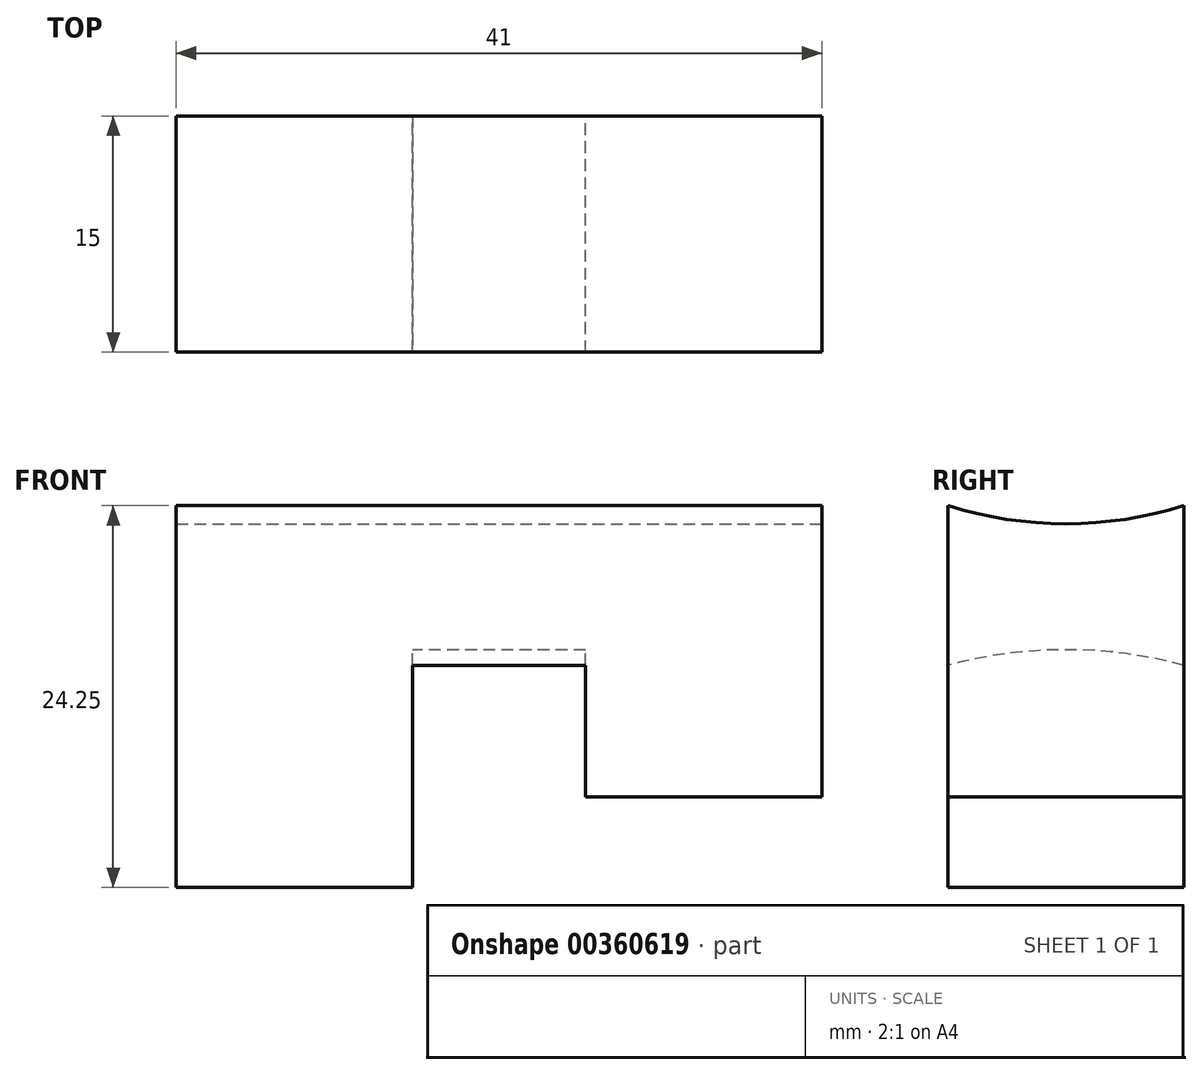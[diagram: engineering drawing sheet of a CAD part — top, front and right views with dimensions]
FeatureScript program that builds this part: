
annotation { "Feature Type Name" : "Feature", "Feature Type Description" : "" }
export const myFeature = defineFeature(function(context is Context, id is Id, definition is map)
    precondition{}
    {
        {
            var Q0;
            Q0=qCreatedBy(makeId("Top.planeOp"),FACE);
            var sketch = newSketch(context, id + "F0", { "sketchPlane" : qUnion([Q0])});
            skLineSegment(sketch, "E0.bottom", {"start": v(-5.5, 7.5) * mm, "end": v(5.5, 7.5) * mm});
            skLineSegment(sketch, "E0.top", {"start": v(-5.5, -7.5) * mm, "end": v(5.5, -7.5) * mm});
            skLineSegment(sketch, "E0.left", {"start": v(-5.5, 7.5) * mm, "end": v(-5.5, -7.5) * mm});
            skLineSegment(sketch, "E0.right", {"start": v(5.5, 7.5) * mm, "end": v(5.5, -7.5) * mm});
            skPoint(sketch, "E0.middle", {"position": v(0, 0) * mm});
            skSolve(sketch);
        }
        {
            var Q0;
            Q0 = qSketchRegion(id + "F0", true);
            extrude(context, id + "F1", {"entities" : qUnion([Q0]), "depth" : 20 * mm});
        }
        {
            var Q0;
            Q0=makeQuery(id+"F1.opExtrude","SWEPT_FACE",FACE,{"disambiguationData":[OSD([sQuery(id+"F0.wireOp",EDGE,"E0.left")])]});
            var sketch = newSketch(context, id + "F2", { "sketchPlane" : qUnion([Q0])});
            skLineSegment(sketch, "E1", {"start": v(0, 20) * mm, "end": v(0, -25) * mm});
            skCircle(sketch, "E2", {"center": v(0, -25) * mm, "radius": 29 * mm});
            skSolve(sketch);
        }
        {
            var Q0;
            Q0 = qSketchRegion(id + "F2", true);
            extrude(context, id + "F3", {"entities" : qUnion([Q0]), "operationType" : NewBodyOperationType.REMOVE, "oppositeDirection" : true, "depth" : 11 * mm});
        }
        {
            var Q0;
            Q0=makeQuery(id+"F1.opExtrude","SWEPT_FACE",FACE,{"disambiguationData":[OSD([sQuery(id+"F0.wireOp",EDGE,"E0.left")])]});
            var sketch = newSketch(context, id + "F4", { "sketchPlane" : qUnion([Q0])});
            skLineSegment(sketch, "E3.bottom", {"start": v(-7.5, 20) * mm, "end": v(7.5, 20) * mm});
            skLineSegment(sketch, "E3.top", {"start": v(-7.5, -11.1) * mm, "end": v(7.5, -11.1) * mm});
            skLineSegment(sketch, "E3.left", {"start": v(-7.5, 20) * mm, "end": v(-7.5, -11.1) * mm});
            skLineSegment(sketch, "E3.right", {"start": v(7.5, 20) * mm, "end": v(7.5, -11.1) * mm});
            skLineSegment(sketch, "E4", {"start": v(0, 20) * mm, "end": v(0, -25) * mm});
            skPoint(sketch, "E4.endSnap0", {"position": v(0, -11.1) * mm});
            skCircle(sketch, "E5", {"center": v(0, -25) * mm, "radius": 26 * mm});
            skSolve(sketch);
        }
        {
            var Q0;
            {var subQ0=sQuery(id+"F4.wireOp",EDGE,"E3.left");var subQ1=sQuery(id+"F4.wireOp",EDGE,"E3.bottom");var subQ2=makeQuery(id+"F4.imprint","INTERSECT",VERTEX,{"derivedFrom":[subQ1,subQ0]});Q0=makeQuery(id+"F4.imprint","IMPRINT",FACE,{"disambiguationData":[TD([[makeQuery(id+"F4.imprint","IMPRINT",EDGE,{"disambiguationData":[TD([[subQ2,-1.0]])],"derivedFrom":subQ1}),-1.0]])]});}
            var Q1;
            {var subQ0=sQuery(id+"F4.wireOp",EDGE,"E3.right");var subQ1=sQuery(id+"F4.wireOp",EDGE,"E3.bottom");var subQ2=makeQuery(id+"F4.imprint","INTERSECT",VERTEX,{"derivedFrom":[subQ1,subQ0]});Q1=makeQuery(id+"F4.imprint","IMPRINT",FACE,{"disambiguationData":[TD([[makeQuery(id+"F4.imprint","IMPRINT",EDGE,{"disambiguationData":[TD([[subQ2,1.0]])],"derivedFrom":subQ1}),-1.0]])]});}
            var Q2;
            {var subQ0=sQuery(id+"F4.wireOp",EDGE,"E3.left");var subQ1=makeQuery(id+"F3.boolean.opBoolean","COPY",EDGE,{"derivedFrom":makeQuery(id+"F3.opExtrude","CAP_EDGE",EDGE,{"disambiguationData":[OSD([sQuery(id+"F2.wireOp",EDGE,"E2")])],"isStart":true})});var subQ2=makeQuery(id+"F4.imprint","INTERSECT",VERTEX,{"derivedFrom":[subQ1,subQ0]});Q2=makeQuery(id+"F4.imprint","IMPRINT",FACE,{"disambiguationData":[TD([[makeQuery(id+"F4.imprint","IMPRINT",EDGE,{"disambiguationData":[TD([[subQ2,-1.0]])],"derivedFrom":subQ0}),1.0]])]});}
            var Q3;
            {var subQ0=sQuery(id+"F4.wireOp",EDGE,"E3.right");var subQ1=makeQuery(id+"F3.boolean.opBoolean","COPY",EDGE,{"derivedFrom":makeQuery(id+"F3.opExtrude","CAP_EDGE",EDGE,{"disambiguationData":[OSD([sQuery(id+"F2.wireOp",EDGE,"E2")])],"isStart":true})});var subQ2=makeQuery(id+"F4.imprint","INTERSECT",VERTEX,{"derivedFrom":[subQ1,subQ0]});Q3=makeQuery(id+"F4.imprint","IMPRINT",FACE,{"disambiguationData":[TD([[makeQuery(id+"F4.imprint","IMPRINT",EDGE,{"disambiguationData":[TD([[subQ2,-1.0]])],"derivedFrom":subQ0}),-1.0]])]});}
            extrude(context, id + "F5", {"entities" : qUnion([Q0, Q1, Q2, Q3]), "operationType" : NewBodyOperationType.ADD, "depth" : 15 * mm});
        }
        {
            var Q0;
            Q0=makeQuery(id+"F1.opExtrude","SWEPT_FACE",FACE,{"disambiguationData":[OSD([sQuery(id+"F0.wireOp",EDGE,"E0.right")])]});
            var sketch = newSketch(context, id + "F6", { "sketchPlane" : qUnion([Q0])});
            skLineSegment(sketch, "E6.bottom", {"start": v(-7.5, 20) * mm, "end": v(7.5, 20) * mm});
            skLineSegment(sketch, "E6.top", {"start": v(-7.5, -5.34) * mm, "end": v(7.5, -5.34) * mm});
            skLineSegment(sketch, "E6.left", {"start": v(-7.5, 20) * mm, "end": v(-7.5, -5.34) * mm});
            skLineSegment(sketch, "E6.right", {"start": v(7.5, 20) * mm, "end": v(7.5, -5.34) * mm});
            skLineSegment(sketch, "E7", {"start": v(0, 20) * mm, "end": v(0, -25) * mm});
            skPoint(sketch, "E7.endSnap0", {"position": v(0, 20) * mm});
            skCircle(sketch, "E8", {"center": v(0, -25) * mm, "radius": 28 * mm});
            skSolve(sketch);
        }
        {
            var Q0;
            {var subQ0=sQuery(id+"F6.wireOp",EDGE,"E6.left");var subQ1=sQuery(id+"F6.wireOp",EDGE,"E6.bottom");var subQ2=makeQuery(id+"F6.imprint","INTERSECT",VERTEX,{"derivedFrom":[subQ1,subQ0]});Q0=makeQuery(id+"F6.imprint","IMPRINT",FACE,{"disambiguationData":[TD([[makeQuery(id+"F6.imprint","IMPRINT",EDGE,{"disambiguationData":[TD([[subQ2,1.0]])],"derivedFrom":subQ1}),1.0]])]});}
            var Q1;
            {var subQ0=sQuery(id+"F6.wireOp",EDGE,"E6.left");var subQ1=makeQuery(id+"F3.boolean.opBoolean","COPY",EDGE,{"derivedFrom":makeQuery(id+"F3.opExtrude","CAP_EDGE",EDGE,{"disambiguationData":[OSD([sQuery(id+"F2.wireOp",EDGE,"E2")])],"isStart":false})});var subQ2=makeQuery(id+"F6.imprint","INTERSECT",VERTEX,{"derivedFrom":[subQ1,subQ0]});Q1=makeQuery(id+"F6.imprint","IMPRINT",FACE,{"disambiguationData":[TD([[makeQuery(id+"F6.imprint","IMPRINT",EDGE,{"disambiguationData":[TD([[subQ2,-1.0]])],"derivedFrom":subQ0}),1.0]])]});}
            var Q2;
            {var subQ0=sQuery(id+"F6.wireOp",EDGE,"E6.right");var subQ1=makeQuery(id+"F3.boolean.opBoolean","COPY",EDGE,{"derivedFrom":makeQuery(id+"F3.opExtrude","CAP_EDGE",EDGE,{"disambiguationData":[OSD([sQuery(id+"F2.wireOp",EDGE,"E2")])],"isStart":false})});var subQ2=makeQuery(id+"F6.imprint","INTERSECT",VERTEX,{"derivedFrom":[subQ1,subQ0]});Q2=makeQuery(id+"F6.imprint","IMPRINT",FACE,{"disambiguationData":[TD([[makeQuery(id+"F6.imprint","IMPRINT",EDGE,{"disambiguationData":[TD([[subQ2,-1.0]])],"derivedFrom":subQ0}),-1.0]])]});}
            var Q3;
            {var subQ0=sQuery(id+"F6.wireOp",EDGE,"E6.right");var subQ1=sQuery(id+"F6.wireOp",EDGE,"E6.bottom");var subQ2=makeQuery(id+"F6.imprint","INTERSECT",VERTEX,{"derivedFrom":[subQ1,subQ0]});Q3=makeQuery(id+"F6.imprint","IMPRINT",FACE,{"disambiguationData":[TD([[makeQuery(id+"F6.imprint","IMPRINT",EDGE,{"disambiguationData":[TD([[subQ2,-1.0]])],"derivedFrom":subQ1}),1.0]])]});}
            extrude(context, id + "F7", {"entities" : qUnion([Q0, Q1, Q2, Q3]), "operationType" : NewBodyOperationType.ADD, "depth" : 15 * mm});
        }
        {
            var Q0;
            Q0=makeQuery(id+"F7.opExtrude","CAP_FACE",FACE,{"disambiguationData":[OSD([sQuery(id+"F6.wireOp",EDGE,"E6.bottom"),sQuery(id+"F6.wireOp",EDGE,"E6.left"),sQuery(id+"F6.wireOp",EDGE,"E6.right"),sQuery(id+"F6.wireOp",EDGE,"E8")])],"isStart":false});
            var sketch = newSketch(context, id + "F8", { "sketchPlane" : qUnion([Q0])});
            skLineSegment(sketch, "E9", {"start": v(0, 0) * mm, "end": v(0, 12) * mm});
            skLineSegment(sketch, "E10", {"start": v(0, 12) * mm, "end": v(0, 37) * mm});
            skCircle(sketch, "E11", {"center": v(0, 37) * mm, "radius": 25 * mm});
            skSolve(sketch);
        }
        {
            var Q0;
            Q0 = qSketchRegion(id + "F8", true);
            extrude(context, id + "F9", {"entities" : qUnion([Q0]), "operationType" : NewBodyOperationType.REMOVE, "oppositeDirection" : true, "depth" : 54.1 * mm});
        }
    });
